# Revit family: EC-11-TY5237_Metric
name_source: partatom
category: Sprinklers
units: mm (PartAtom-declared; Revit-internal decimal feet)

## family parameters
Always vertical = Yes
Cut with Voids When Loaded = No
Maintain Annotation Orientation = No
OmniClass Number = 23.65.70.17.11.24
OmniClass Title = Fire Fighting Sprinkler Heads
Part Type = Normal
Room Calculation Point = No
Round Connector Dimension = Use Diameter
Shared = No
Work Plane-Based = No

## types (22) — shared parameters
COBie = Yes
COBie.Component.Name = Sprinklers:Pendent_SIN
COBie.Type = Yes
COBie.Type.AssetType = Fixed
COBie.Type.Category = Pr_70_55_97_84:Sprinklers
COBie.Type.Manufacturer = Tyco Fire Protection Products
COBie.Type.Material = Bronze
COBie.Type.Shape = Cylinder
Coverage = Extended
Coverage_ = Extended
K-Factor = 159.8191
Manufacturer = Tyco Fire Protection Products
Manufacturer URL = www.tyco-fire.com
Material_ = Bronze
Model = EC-11
Nominal Diameter 1 = 20 mm
Orifice = Extra Large
Orifice Size = 3 mm
Outside Diameter 1 = 27 mm
Response = Quick
Response_ = Quick
SIN No = TY5237
Takeout 1 = 62 mm
Technical Data Sheet No = TFP220
zero-valued in all types: COBie.Type.NominalHeight, COBie.Type.NominalLength, COBie.Type.NominalWidth, COBie.Type.ReplacementCost, Default Elevation, Style Id

## per-type parameters (varying)
| type | COBie.Component.Description | COBie.Type.Colour | COBie.Type.DurationUnit | COBie.Type.Finish | COBie.Type.ModelNumber | COBie.Type.ModelReference | COBie.Type.Size | COBie.Type.WarrantyDurationParts | COBie.Type.WarrantyGuarantorLabor | COBie.Type.WarrantyGuarantorParts | Description | Finish_ | Part No | Temperature Rating |
| EC-11 Wet Pendent_135  57.2°C K160 DN20 NPT Br_51-893-1-135 | EC-11 Wet Pendent  135°F K11.2 3/4 NPT Br | Yellow | year | Natural Brass | 51-893-1-135 | EC-11 Wet Pendent  135°F K11.2 3/4 NPT Br | 3/4"(DN20) |  |  | http://tycofsbp.com | EC-11 Wet Pendent_Yellow_135  57.2°C K160 DN20 NPT Br | Natural Brass | 51-893-1-135 | 57 °C |
| EC-11 Wet Pendent_155  68.3°C K160 DN20 NPT Br_51-893-1-155 | EC-11 Wet Pendent  68.3°C K160 DN20 NPT Br | Yellow | year | Natural Brass | 51-893-1-155 | EC-11 Wet Pendent  68.3°C K160 DN20 NPT Br | 3/4"(DN20) |  |  | http://tycofsbp.com | EC-11 Wet Pendent_Yellow_155  68.3°C K160 DN20 NPT Br | Natural Brass | 51-893-1-155 | 68 °C |
| EC-11 Wet Pendent_175  79.4°C K160 DN20 NPT Br_51-893-1-175 | EC-11 Wet Pendent  79.4°C K160 DN20 NPT Br | Yellow | year | Natural Brass | 51-893-1-175 | EC-11 Wet Pendent  79.4°C K160 DN20 NPT Br | 3/4"(DN20) |  |  | http://tycofsbp.com | EC-11 Wet Pendent_Yellow_175  79.4°C K160 DN20 NPT Br | Natural Brass | 51-893-1-175 | 79 °C |
| EC-11 Wet Pendent_200  93.3°C K160 DN20 NPT Br_51-893-1-200 | EC-11 Wet Pendent  93.3°C K160 DN20 NPT Br | Yellow | Year | Natural Brass | 51-893-1-200 | EC-11 Wet Pendent  93.3°C K160 DN20 NPT Br | 3/4"(DN20) |  |  | http://tycofsbp.com | EC-11 Wet Pendent_Yellow_200  93.3°C K160 DN20 NPT Br | Natural Brass | 51-893-1-200 | 93 °C |
| EC-11 Wet Pendent_286  141.1°C K160 DN20 NPT Br_51-893-1-286 | EC-11 Wet Pendent  141.1°C K160 DN20 NPT Br | Yellow | year | Natural Brass | 51-893-1-286 | EC-11 Wet Pendent  141.1°C K160 DN20 NPT Br | 3/4"(DN20) |  |  | http://tycofsbp.com | EC-11 Wet Pendent_Yellow_286  141.1°C K160 DN20 NPT Br | Natural Brass | 51-893-1-286 | 141 °C |
| EC-11 Wet Pendent_135  57.2°C K160 DN20 NPT Wh9003PE_51-893-4-135 | EC-11 Wet Pendent  57.2°C K160 DN20 NPT Wh9003PE | White | year | Signal White | 51-893-4-135 | EC-11 Wet Pendent  57.2°C K160 DN20 NPT Wh9003PE | 3/4"(DN20) |  |  | http://tycofsbp.com | EC-11 Wet Pendent_White_135  57.2°C K160 DN20 NPT Wh9003PE | White RAL9003 | 51-893-4-135 | 57 °C |
| EC-11 Wet Pendent_155  68.3°C K160 DN20 NPT Wh9003PE_51-893-4-155 | EC-11 Wet Pendent  68.3°C K160 DN20 NPT Wh9003PE | White | year | Signal White | 51-893-4-155 | EC-11 Wet Pendent  68.3°C K160 DN20 NPT Wh9003PE | 3/4"(DN20) |  |  | http://tycofsbp.com | EC-11 Wet Pendent_White_155  68.3°C K160 DN20 NPT Wh9003PE | White RAL9003 | 51-893-4-155 | 68 °C |
| EC-11 Wet Pendent_175  79.4°C K160 DN20 NPT Wh9003PE_51-893-4-175 | EC-11 Wet Pendent  79.4°C K160 DN20 NPT Wh9003PE | White | year | Signal White | 51-893-4-175 | EC-11 Wet Pendent  79.4°C K160 DN20 NPT Wh9003PE | 3/4"(DN20) |  |  | http://tycofsbp.com | EC-11 Wet Pendent_White_175  79.4°C K160 DN20 NPT Wh9003PE | White RAL9003 | 51-893-4-175 | 79 °C |
| EC-11 Wet Pendent_200  93.3°C K160 DN20 NPT Wh9003PE_51-893-4-200 | EC-11 Wet Pendent  93.3°C K160 DN20 NPT Wh9003PE | White | year | Signal White | 51-893-4-200 | EC-11 Wet Pendent  93.3°C K160 DN20 NPT Wh9003PE | 3/4"(DN20) |  |  | http://tycofsbp.com | EC-11 Wet Pendent_White_200  93.3°C K160 DN20 NPT Wh9003PE | White RAL9003 | 51-893-4-200 | 93 °C |
| EC-11 Wet Pendent_286  141.1°C K160 DN20 NPT Wh9003PE_51-893-4-286 | EC-11 Wet Pendent  141.1°C K160 DN20 NPT Wh9003PE | White | year | Signal White | 51-893-4-286 | EC-11 Wet Pendent  141.1°C K160 DN20 NPT Wh9003PE | 3/4"'(DN20) |  |  | http://tycofsbp.com | EC-11 Wet Pendent_White_286  141.1°C K160 DN20 NPT Wh9003PE | White RAL9003 | 51-893-4-286 | 141 °C |
| EC-11 Wet Pendent_155   68.3°C K160 DN20 NPT JBlk_51-893-5-155 | EC-11 Wet Pendent_White_155  68.3°C K160 DN20 NPT Wh9003PE | Black | year | Jet Black | 51-893-5-155 | EC-11 Wet Pendent_White_155  68.3°C K160 DN20 NPT Wh9003PE | 3/4"(DN20) |  |  | http://tycofsbp.com | EC-11 Wet Pendent_Black_155   68.3°C K160 DN20 NPT JBlk | Jet Black RAL9005 | 51-893-5-155 | 68 °C |
| EC-11 Wet Pendent_200  68.3°C K160 DN20 NPT JBlk_51-893-5-200 | EC-11 Wet Pendent_Black_155   68.3°C K160 DN20 NPT Wh9003PE | Black | year | Jet Black | 51-893-5-200 | EC-11 Wet Pendent_Black_155   68.3°C K160 DN20 NPT Wh9003PE | 3/4"(DN20) |  |  | http://tycofsbp.com | EC-11 Wet Pendent_Black_200  68.3°C K160 DN20 NPT JBlk | Jet Black RAL9005 | 51-893-5-200 | 93 °C |
| EC-11 Wet Pendent_135  57.2°C K160 DN20 NPT Lead_51-893-7-135 | EC-11 Wet Pendent  57.2°C K160 DN20 NPT LeadCt | Gray | year | Lead Coated | 51-893-7-135 | EC-11 Wet Pendent  57.2°C K160 DN20 NPT LeadCt | 3/4"(DN20) |  |  | http://tycofsbp.com | EC-11 Wet Pendent_Gray_135  57.2°C K160 DN20 NPT Lead | Lead Coated | 51-893-7-135 | 57 °C |
| EC-11 Wet Pendent_155  68.3°C K160 DN20 NPT Lead_51-893-7-155 | EC-11 Wet Pendent  68.3°C K160 DN20 NPT LeadCt | Gray | year | Lead Coated | 51-893-7-155 | EC-11 Wet Pendent  68.3°C K160 DN20 NPT LeadCt | 3/4"(DN20) | 10 | http://tycofsbp.com |  | EC-11 Wet Pendent_Gray_155  68.3°C K160 DN20 NPT Lead | Lead Coated | 51-893-7-155 | 68 °C |
| EC-11 Wet Pendent_175  79.4°C K160 DN20 NPT Lead_51-893-7-175 | EC-11 Wet Pendent  79.4°C K160 DN20 NPT LeadCt | Gray | year | Lead Coated | 51-893-7-175 | EC-11 Wet Pendent  79.4°C K160 DN20 NPT LeadCt | 3/4"(DN20) |  |  | http://tycofsbp.com | EC-11 Wet Pendent_Gray_175  79.4°C K160 DN20 NPT Lead | Lead Coated | 51-893-7-175 | 79 °C |
| EC-11 Wet Pendent_200  93.3°C K160 DN20 NPT Lead_51-893-7-200 | EC-11 Wet Pendent  93.3°C K160 DN20 NPT LeadCt | Gray | year | Lead Coated | 51-893-7-200 | EC-11 Wet Pendent  93.3°C K160 DN20 NPT LeadCt | 3/4"(DN20) |  |  | http://tycofsbp.com | EC-11 Wet Pendent_Gray_200  93.3°C K160 DN20 NPT Lead | Lead Coated | 51-893-7-200 | 93 °C |
| EC-11 Wet Pendent_286  141.1°C K160 DN20 NPT Lead_51-893-7-286 | EC-11 Wet Pendent  141.1°C K160 DN20 NPT LeadCt | Gray | year | Lead Coated | 51-893-7-286 | EC-11 Wet Pendent  141.1°C K160 DN20 NPT LeadCt | 3/4"(DN20) |  |  | http://tycofsbp.com | EC-11 Wet Pendent_Gray_286  141.1°C K160 DN20 NPT Lead | Lead Coated | 51-893-7-286 | 141 °C |
| EC-11 Wet Pendent_135  57.2°C K160 DN20 NPT Chr_51-893-9-135 | EC-11 Wet Pendent  57.2°C K160 DN20 NPT Chr | Silver | year | Chrome Plated | 51-893-9-135 | EC-11 Wet Pendent  57.2°C K160 DN20 NPT Chr | 3/4"(DN20) |  |  | http://tycofsbp.com | EC-11 Wet Pendent_Silver_135  57.2°C K160 DN20 NPT Chr | Chrome Plated | 51-893-9-135 | 57 °C |
| EC-11 Wet Pendent_155  68.3°C K160 DN20 NPT Chr_51-893-9-155 | EC-11 Wet Pendent  68.3°C K160 DN20 NPT Chr | Silver | year | Chrome Plated | 51-893-9-155 | EC-11 Wet Pendent  68.3°C K160 DN20 NPT Chr | 3/4"(DN20) |  |  | http://tycofsbp.com | EC-11 Wet Pendent_Silver_155  68.3°C K160 DN20 NPT Chr | Chrome Plated | 51-893-9-155 | 68 °C |
| EC-11 Wet Pendent_175  79.4°C K160 DN20 NPT Chr_51-893-9-175 | EC-11 Wet Pendent  79.4°C K160 DN20 NPT Chr | Silver | year | Chrome Plated | 51-893-9-175 | EC-11 Wet Pendent  79.4°C K160 DN20 NPT Chr | (DN20) |  |  | http://tycofsbp.com | EC-11 Wet Pendent_Silver_175  79.4°C K160 DN20 NPT Chr | Chrome Plated | 51-893-9-175 | 79 °C |
| EC-11 Wet Pendent_200  93.3°C K160 DN20 NPT Chr_51-893-9-200 | EC-11 Wet Pendent  93.3°C K160 DN20 NPT Chr | Silver | year | Chrome Plated | 51-893-9-200 | EC-11 Wet Pendent  93.3°C K160 DN20 NPT Chr | 3/4"(DN20) |  |  | http://tycofsbp.com | EC-11 Wet Pendent_Silver_200  93.3°C K160 DN20 NPT Chr | Chrome Plated | 51-893-9-200 | 93 °C |
| EC-11 Wet Pendent_286  141.1°C K160 DN20 NPT Chr_51-893-9-286 | EC-11 Wet Pendent  141.1°C K160 DN20 NPT Chr | Silver | year | Chrome Plated | 51-893-9-286 | EC-11 Wet Pendent  141.1°C K160 DN20 NPT Chr | 3/4"(DN20) |  |  | http://tycofsbp.com | EC-11 Wet Pendent_Silver_286  141.1°C K160 DN20 NPT Chr | Chrome Plated | 51-893-9-286 | 141 °C |

## geometry (parser evidence)
native form markers: Blend x2, Sweep x48
no freeform markers — native parametric forms only
